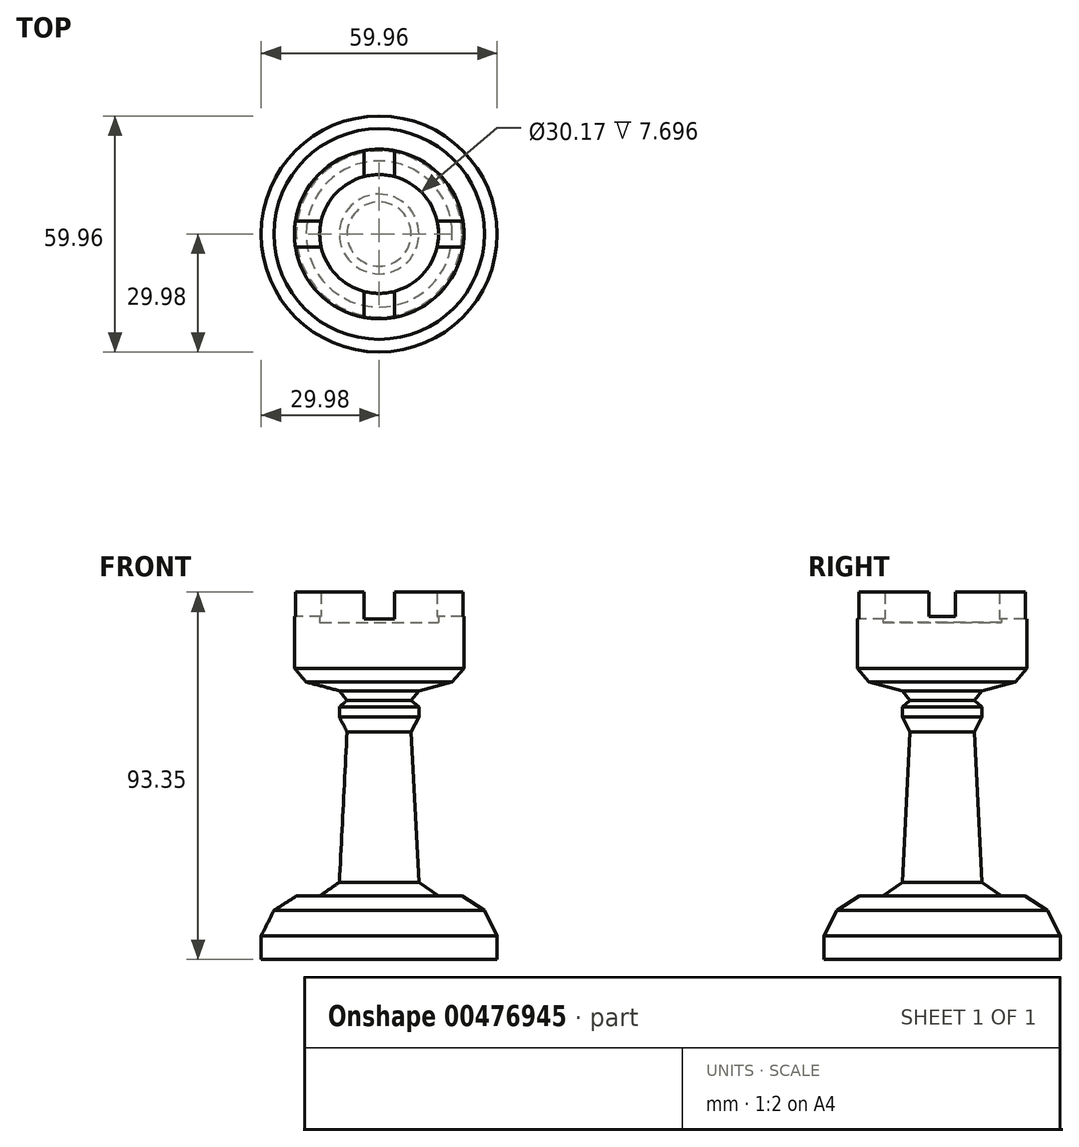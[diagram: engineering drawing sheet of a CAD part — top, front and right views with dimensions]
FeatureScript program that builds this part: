
annotation { "Feature Type Name" : "Feature", "Feature Type Description" : "" }
export const myFeature = defineFeature(function(context is Context, id is Id, definition is map)
    precondition{}
    {
        {
            var Q0;
            Q0=qCreatedBy(makeId("Front.planeOp"),FACE);
            var sketch = newSketch(context, id + "F0", { "sketchPlane" : qUnion([Q0])});
            skLineSegment(sketch, "E0", {"start": v(0, 24.07) * mm, "end": v(-15.09, 24.07) * mm});
            skLineSegment(sketch, "E1", {"start": v(-15.09, 24.07) * mm, "end": v(-15.09, 31.77) * mm});
            skLineSegment(sketch, "E2", {"start": v(-15.09, 31.77) * mm, "end": v(-21.54, 31.77) * mm});
            skLineSegment(sketch, "E3", {"start": v(-21.54, 31.77) * mm, "end": v(-21.54, 12.4) * mm});
            skLineSegment(sketch, "E4", {"start": v(-21.54, 12.4) * mm, "end": v(-18.56, 8.93) * mm});
            skLineSegment(sketch, "E5", {"start": v(-18.56, 8.93) * mm, "end": v(-10.12, 6.7) * mm});
            skLineSegment(sketch, "E6", {"start": v(-10.12, 6.7) * mm, "end": v(-8.13, 4.21) * mm});
            skLineSegment(sketch, "E7", {"start": v(-8.13, 4.21) * mm, "end": v(-10.12, 2.62) * mm});
            skLineSegment(sketch, "E8", {"start": v(-10.12, 2.62) * mm, "end": v(-10.12, 0) * mm});
            skLineSegment(sketch, "E9", {"start": v(-10.12, 0) * mm, "end": v(-8.13, -3.73) * mm});
            skLineSegment(sketch, "E10", {"start": v(-8.13, -3.73) * mm, "end": v(-10.12, -41.96) * mm});
            skLineSegment(sketch, "E11", {"start": v(-10.12, -41.96) * mm, "end": v(-15.09, -45.44) * mm});
            skLineSegment(sketch, "E12", {"start": v(-15.09, -45.44) * mm, "end": v(-21.04, -45.44) * mm});
            skLineSegment(sketch, "E13", {"start": v(-21.04, -45.44) * mm, "end": v(-26.75, -49.16) * mm});
            skLineSegment(sketch, "E14", {"start": v(-26.75, -49.16) * mm, "end": v(-29.98, -55.62) * mm});
            skLineSegment(sketch, "E15", {"start": v(-29.98, -55.62) * mm, "end": v(-29.98, -61.58) * mm});
            skLineSegment(sketch, "E16", {"start": v(-29.98, -61.58) * mm, "end": v(0, -61.58) * mm});
            skLineSegment(sketch, "E17", {"start": v(0, -61.58) * mm, "end": v(0, 24.07) * mm});
            skSolve(sketch);
        }
        {
            var Q0;
            Q0 = qSketchRegion(id + "F0", true);
            var Q1;
            Q1=sQuery(id+"F0.wireOp",EDGE,"E17");
            revolve(context, id + "F1", {"entities" : qUnion([Q0]), "axis" : qUnion([Q1]), "revolveType" : RevolveType.FULL});
        }
        {
            var Q0;
            Q0=qCreatedBy(makeId("Front.planeOp"),FACE);
            var sketch = newSketch(context, id + "F2", { "sketchPlane" : qUnion([Q0])});
            skLineSegment(sketch, "E18.bottom", {"start": v(3.85, 24.93) * mm, "end": v(-3.85, 24.93) * mm});
            skLineSegment(sketch, "E18.top", {"start": v(3.85, 39.44) * mm, "end": v(-3.85, 39.44) * mm});
            skLineSegment(sketch, "E18.left", {"start": v(3.85, 24.93) * mm, "end": v(3.85, 39.44) * mm});
            skLineSegment(sketch, "E18.right", {"start": v(-3.85, 24.93) * mm, "end": v(-3.85, 39.44) * mm});
            skPoint(sketch, "E18.middle", {"position": v(0, 32.19) * mm});
            skSolve(sketch);
        }
        {
            var Q0;
            Q0 = qSketchRegion(id + "F2", true);
            extrude(context, id + "F3", {"entities" : qUnion([Q0]), "operationType" : NewBodyOperationType.REMOVE, "endBound" : BoundingType.THROUGH_ALL, "oppositeDirection" : true, "depth" : 25.4 * mm, "hasSecondDirection" : true, "secondDirectionOppositeDirection" : false, "secondDirectionDepth" : 25.4 * mm});
        }
        {
            var Q0;
            Q0=qCreatedBy(makeId("Right.planeOp"),FACE);
            var sketch = newSketch(context, id + "F4", { "sketchPlane" : qUnion([Q0])});
            skLineSegment(sketch, "E19.bottom", {"start": v(3.3, 25.53) * mm, "end": v(-3.3, 25.53) * mm});
            skLineSegment(sketch, "E19.top", {"start": v(3.3, 38.22) * mm, "end": v(-3.3, 38.22) * mm});
            skLineSegment(sketch, "E19.left", {"start": v(3.3, 25.53) * mm, "end": v(3.3, 38.22) * mm});
            skLineSegment(sketch, "E19.right", {"start": v(-3.3, 25.53) * mm, "end": v(-3.3, 38.22) * mm});
            skPoint(sketch, "E19.middle", {"position": v(0, 31.88) * mm});
            skSolve(sketch);
        }
        {
            var Q0;
            Q0 = qSketchRegion(id + "F4", true);
            extrude(context, id + "F5", {"entities" : qUnion([Q0]), "operationType" : NewBodyOperationType.REMOVE, "endBound" : BoundingType.THROUGH_ALL, "depth" : 25.4 * mm, "hasSecondDirection" : true, "secondDirectionOppositeDirection" : true, "secondDirectionDepth" : 25.4 * mm});
        }
    });
